# Revit family: KEUCO_59552019502
name_source: partatom
category: Allgemeines Modell
revit_build: Autodesk Revit 2016 (Build: 20150220_1215(x64)
units: mm (PartAtom-declared; Revit-internal decimal feet)

## family parameters
Arbeitsebenenbasiert = Ja
Beim Laden mit Abzugskörper schneiden = Nein
Bemaßung runder Anschluss = Durchmesser verwenden
Gemeinsam genutzt = Nein
Immer vertikal = Nein
Kann Basisbauteil für Bewehrung sein = Nein
Raumberechnungspunkt = Nein
Teiletyp = Normal

## types (1)
- 59552019502
    Artikelnummer = 59552019502
    Ausschreibungstext = KEUCO  IXMO - SOLO Einhebelmischer 59552019502
Einhebelmischer mit integriertem Schlauchanschluss UP DN15
Hochglanzverchromter Einhebelmischer mit Schlauchanschluss für die Dusche 
aus entzinkungsarmen Messing, mit eckiger Rosette, frei positionierbar,
Integrierter Einbautiefenausgleich von 65-95mm, Gehäuse schallentkoppelt,
Hochwertige Mischwasserkartusche mit keramischen Dichtscheiben und Temperaturbegrenzung,
Fertigset bestehend aus:
Hebel, Hülse, Rosette (eckig) und Funktionseinheit,
Gesamthöhe mit Griff 130 mm, Rosettendurchmesser 90 mm,
Stärke 10 mm, Gesamtausladung 89 mm
passend für UP-Funktionseinheit Artikel-Nr. 59552000170
    Beschreibung = Mischwasserkartusche mit keramischen Dichtscheiben,
Temperaturbegrenzung und Durchflussbegrenzung,
Schlauchanschluss eigensicher gegen Rückfließen
nach DIN EN 1717
Fertigset bestehend aus:
Hebel, Gehäuse und Rosette (eckig), passend für
UP Funktionseinheit Art. Nr. 59552 000170
    Breite = 45 mm  [stored 0.147638 ft]
    Gewicht = 0
    Hersteller = KEUCO
    Material = Stahl, verchromt
    Serie = Plan
    URL = https://www.keuco.com
    Verwendung = DU / WA
    Vorgabe-Ansicht = 1219 mm

note: [stored X ft] marks values corroborated as IEEE doubles in the binary element streams (Revit-internal decimal feet)

## geometry (parser evidence)
native form markers: Sweep x3
no freeform markers — native parametric forms only
